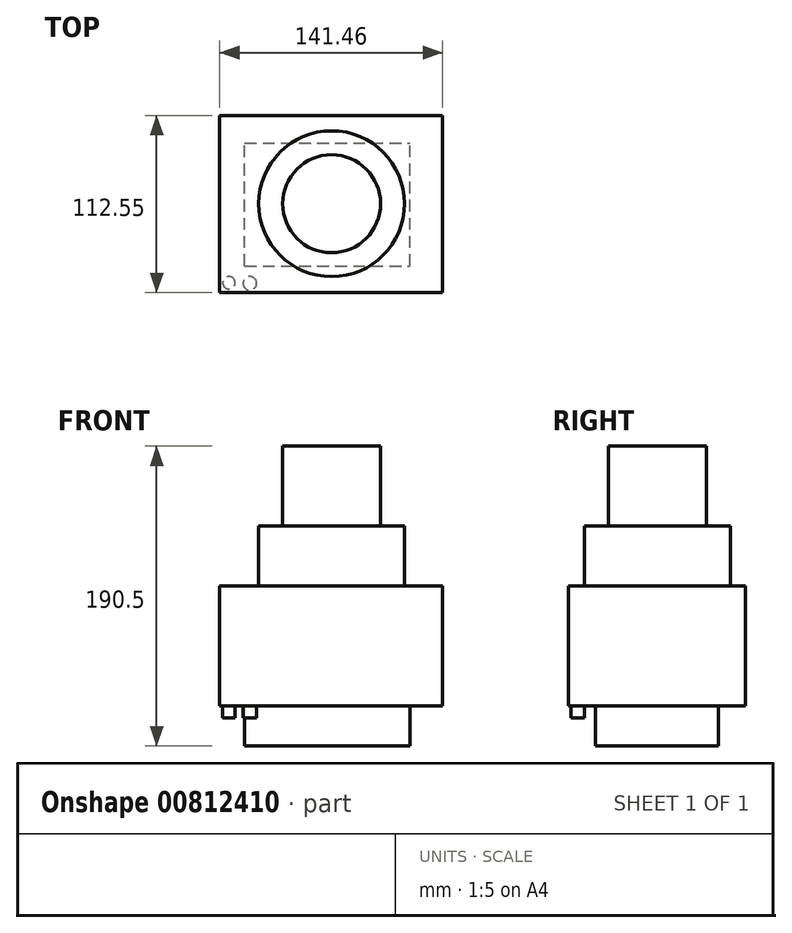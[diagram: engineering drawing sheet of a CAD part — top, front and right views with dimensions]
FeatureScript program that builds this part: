
annotation { "Feature Type Name" : "Feature", "Feature Type Description" : "" }
export const myFeature = defineFeature(function(context is Context, id is Id, definition is map)
    precondition{}
    {
        {
            var Q0;
            Q0=qCreatedBy(makeId("Top.planeOp"),FACE);
            var sketch = newSketch(context, id + "F0", { "sketchPlane" : qUnion([Q0])});
            skCircle(sketch, "E0", {"center": v(0, 0) * mm, "radius": 31.11 * mm});
            skSolve(sketch);
        }
        {
            var Q0;
            Q0 = qSketchRegion(id + "F0", true);
            extrude(context, id + "F1", {"entities" : qUnion([Q0]), "depth" : 50.8 * mm, "offsetDistance" : 25.4 * mm});
        }
        {
            var Q0;
            Q0=makeQuery(id+"F1.opExtrude","CAP_FACE",FACE,{"disambiguationData":[OSD([sQuery(id+"F0.wireOp",EDGE,"E0")])],"isStart":true});
            var sketch = newSketch(context, id + "F2", { "sketchPlane" : qUnion([Q0])});
            skCircle(sketch, "E1", {"center": v(0, 0) * mm, "radius": 46.31 * mm});
            skSolve(sketch);
        }
        {
            var Q0;
            Q0 = qSketchRegion(id + "F2", true);
            extrude(context, id + "F3", {"entities" : qUnion([Q0]), "depth" : 38.1 * mm, "offsetDistance" : 25.4 * mm});
        }
        {
            var Q0;
            Q0=makeQuery(id+"F3.opExtrude","CAP_FACE",FACE,{"disambiguationData":[OSD([sQuery(id+"F2.wireOp",EDGE,"E1")])],"isStart":false});
            var sketch = newSketch(context, id + "F4", { "sketchPlane" : qUnion([Q0])});
            skLineSegment(sketch, "E2.bottom", {"start": v(-71.02, 56.47) * mm, "end": v(70.44, 56.47) * mm});
            skLineSegment(sketch, "E2.top", {"start": v(-71.02, -56.08) * mm, "end": v(70.44, -56.08) * mm});
            skLineSegment(sketch, "E2.left", {"start": v(-71.02, 56.47) * mm, "end": v(-71.02, -56.08) * mm});
            skLineSegment(sketch, "E2.right", {"start": v(70.44, 56.47) * mm, "end": v(70.44, -56.08) * mm});
            skSolve(sketch);
        }
        {
            var Q0;
            Q0 = qSketchRegion(id + "F4", true);
            extrude(context, id + "F5", {"entities" : qUnion([Q0]), "depth" : 76.2 * mm, "offsetDistance" : 25.4 * mm});
        }
        {
            var Q0;
            Q0=makeQuery(id+"F5.opExtrude","CAP_FACE",FACE,{"disambiguationData":[OSD([sQuery(id+"F4.wireOp",EDGE,"E2.bottom"),sQuery(id+"F4.wireOp",EDGE,"E2.top"),sQuery(id+"F4.wireOp",EDGE,"E2.left"),sQuery(id+"F4.wireOp",EDGE,"E2.right")])],"isStart":false});
            var sketch = newSketch(context, id + "F6", { "sketchPlane" : qUnion([Q0])});
            skCircle(sketch, "E3", {"center": v(-65.16, 50.21) * mm, "radius": 3.99 * mm});
            skSolve(sketch);
        }
        {
            var Q0;
            Q0 = qSketchRegion(id + "F6", true);
            extrude(context, id + "F7", {"entities" : qUnion([Q0]), "depth" : 7.62 * mm, "offsetDistance" : 25.4 * mm});
        }
        {
            var Q0;
            Q0=makeQuery(id+"F5.opExtrude","CAP_FACE",FACE,{"disambiguationData":[OSD([sQuery(id+"F4.wireOp",EDGE,"E2.bottom"),sQuery(id+"F4.wireOp",EDGE,"E2.top"),sQuery(id+"F4.wireOp",EDGE,"E2.left"),sQuery(id+"F4.wireOp",EDGE,"E2.right")])],"isStart":false});
            var sketch = newSketch(context, id + "F8", { "sketchPlane" : qUnion([Q0])});
            skCircle(sketch, "E4", {"center": v(-51.87, 50.6) * mm, "radius": 4.32 * mm});
            skSolve(sketch);
        }
        {
            var Q0;
            Q0 = qSketchRegion(id + "F8", true);
            extrude(context, id + "F9", {"entities" : qUnion([Q0]), "depth" : 7.62 * mm, "offsetDistance" : 25.4 * mm});
        }
        {
            var Q0;
            Q0=makeQuery(id+"F5.opExtrude","CAP_FACE",FACE,{"disambiguationData":[OSD([sQuery(id+"F4.wireOp",EDGE,"E2.bottom"),sQuery(id+"F4.wireOp",EDGE,"E2.top"),sQuery(id+"F4.wireOp",EDGE,"E2.left"),sQuery(id+"F4.wireOp",EDGE,"E2.right")])],"isStart":false});
            var sketch = newSketch(context, id + "F10", { "sketchPlane" : qUnion([Q0])});
            skLineSegment(sketch, "E5.bottom", {"start": v(-55.2, 39.47) * mm, "end": v(49.73, 39.47) * mm});
            skLineSegment(sketch, "E5.top", {"start": v(-55.2, -38.69) * mm, "end": v(49.73, -38.69) * mm});
            skLineSegment(sketch, "E5.left", {"start": v(-55.2, 39.47) * mm, "end": v(-55.2, -38.69) * mm});
            skLineSegment(sketch, "E5.right", {"start": v(49.73, 39.47) * mm, "end": v(49.73, -38.69) * mm});
            skSolve(sketch);
        }
        {
            var Q0;
            Q0 = qSketchRegion(id + "F10", true);
            extrude(context, id + "F11", {"entities" : qUnion([Q0]), "depth" : 25.4 * mm, "offsetDistance" : 25.4 * mm});
        }
    });
